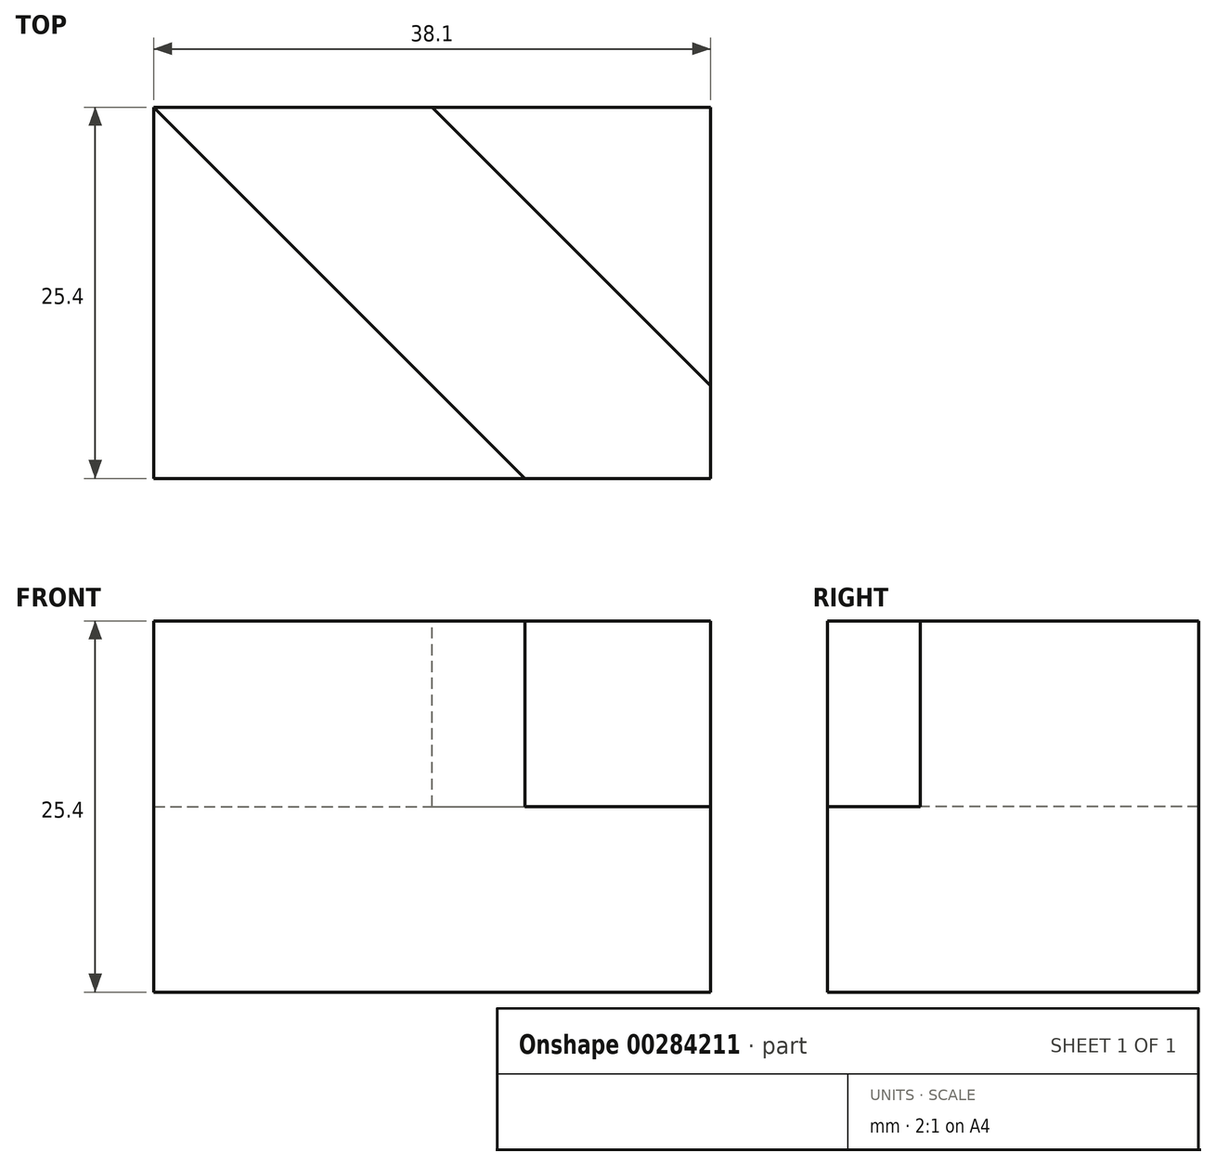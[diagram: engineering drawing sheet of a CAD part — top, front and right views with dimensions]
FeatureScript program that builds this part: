
annotation { "Feature Type Name" : "Feature", "Feature Type Description" : "" }
export const myFeature = defineFeature(function(context is Context, id is Id, definition is map)
    precondition{}
    {
        {
            var Q0;
            Q0=qCreatedBy(makeId("Front.planeOp"),FACE);
            var sketch = newSketch(context, id + "F0", { "sketchPlane" : qUnion([Q0])});
            skLineSegment(sketch, "E0.bottom", {"start": v(0, 0) * mm, "end": v(38.1, 0) * mm});
            skLineSegment(sketch, "E0.top", {"start": v(0, 25.4) * mm, "end": v(38.1, 25.4) * mm});
            skLineSegment(sketch, "E0.left", {"start": v(0, 0) * mm, "end": v(0, 25.4) * mm});
            skLineSegment(sketch, "E0.right", {"start": v(38.1, 0) * mm, "end": v(38.1, 25.4) * mm});
            skSolve(sketch);
        }
        {
            var Q0;
            Q0=makeQuery(id+"F0.imprint","IMPRINT",FACE,{"disambiguationData":[TD([[makeQuery(id+"F0.imprint","IMPRINT",EDGE,{"derivedFrom":sQuery(id+"F0.wireOp",EDGE,"E0.bottom")}),1.0]])]});
            extrude(context, id + "F1", {"entities" : qUnion([Q0]), "depth" : 25.4 * mm});
        }
        {
            var Q0;
            Q0=makeQuery(id+"F1.opExtrude","SWEPT_FACE",FACE,{"disambiguationData":[OSD([sQuery(id+"F0.wireOp",EDGE,"E0.top")])]});
            var sketch = newSketch(context, id + "F2", { "sketchPlane" : qUnion([Q0])});
            skLineSegment(sketch, "E1", {"start": v(0, 0) * mm, "end": v(25.4, -25.4) * mm});
            skLineSegment(sketch, "E2", {"start": v(19.05, 0) * mm, "end": v(38.1, -19.05) * mm});
            skSolve(sketch);
        }
        {
            var Q0;
            {var subQ5=sQuery(id+"F2.wireOp",EDGE,"E1");Q0=makeQuery(id+"F2.imprint","IMPRINT",FACE,{"disambiguationData":[TD([[makeQuery(id+"F2.imprint","IMPRINT",EDGE,{"derivedFrom":subQ5}),1.0]])]});}
            extrude(context, id + "F3", {"entities" : qUnion([Q0]), "operationType" : NewBodyOperationType.REMOVE, "oppositeDirection" : true, "depth" : 12.7 * mm});
        }
    });
